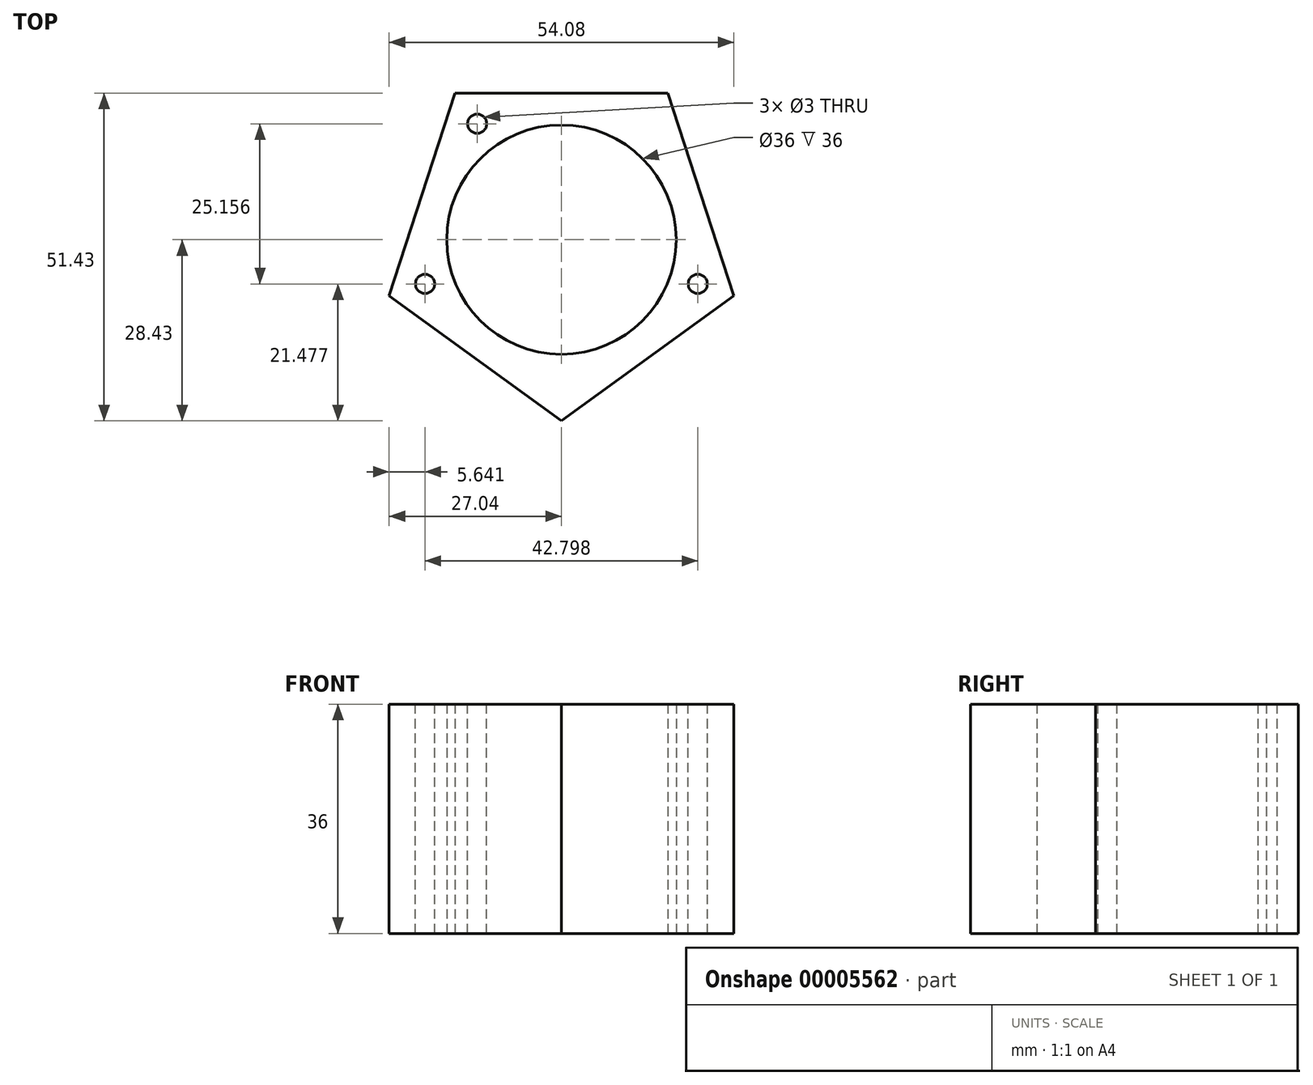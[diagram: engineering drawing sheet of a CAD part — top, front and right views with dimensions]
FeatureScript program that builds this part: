
annotation { "Feature Type Name" : "Feature", "Feature Type Description" : "" }
export const myFeature = defineFeature(function(context is Context, id is Id, definition is map)
    precondition{}
    {
        {
            var Q0;
            Q0=qCreatedBy(makeId("Top.planeOp"),FACE);
            var sketch = newSketch(context, id + "F0", { "sketchPlane" : qUnion([Q0])});
            skCircle(sketch, "E0", {"center": v(0, 0) * mm, "radius": 18 * mm});
            skCircle(sketch, "E1.cCircle", {"center": v(0, 0) * mm, "radius": 23 * mm, "construction": true});
            skLineSegment(sketch, "E1.0", {"start": v(-16.71, 23) * mm, "end": v(16.71, 23) * mm});
            skLineSegment(sketch, "E1.1", {"start": v(16.71, 23) * mm, "end": v(27.04, -8.79) * mm});
            skLineSegment(sketch, "E1.2", {"start": v(27.04, -8.79) * mm, "end": v(0, -28.43) * mm});
            skLineSegment(sketch, "E1.3", {"start": v(0, -28.43) * mm, "end": v(-27.04, -8.79) * mm});
            skLineSegment(sketch, "E1.4", {"start": v(-27.04, -8.79) * mm, "end": v(-16.71, 23) * mm});
            skPoint(sketch, "E1.0.midPoint", {"position": v(0, 23) * mm});
            skSolve(sketch);
        }
        {
            var Q0;
            Q0=qSketchRegion(id+"F0",true);
            extrude(context, id + "F1", {"entities" : qUnion([Q0]), "depth" : 36 * mm});
        }
        {
            var Q0;
            Q0=makeQuery(id+"F1.opExtrude","CAP_FACE",FACE,{"disambiguationData":[OSD([sQuery(id+"F0.wireOp",EDGE,"E0"),sQuery(id+"F0.wireOp",EDGE,"E1.0"),sQuery(id+"F0.wireOp",EDGE,"E1.1"),sQuery(id+"F0.wireOp",EDGE,"E1.2"),sQuery(id+"F0.wireOp",EDGE,"E1.3"),sQuery(id+"F0.wireOp",EDGE,"E1.4")])],"isStart":false});
            var sketch = newSketch(context, id + "F2", { "sketchPlane" : qUnion([Q0])});
            skCircle(sketch, "E2", {"center": v(0, -22.5) * mm, "radius": 1.5 * mm});
            skCircle(sketch, "E3.1.0", {"center": v(-21.4, -6.95) * mm, "radius": 1.5 * mm});
            skCircle(sketch, "E3.2.0", {"center": v(-13.23, 18.2) * mm, "radius": 1.5 * mm});
            skCircle(sketch, "E3.3.0", {"center": v(13.23, 18.2) * mm, "radius": 1.5 * mm});
            skCircle(sketch, "E3.4.0", {"center": v(21.4, -6.95) * mm, "radius": 1.5 * mm});
            skPoint(sketch, "E3.center", {"position": v(0, 0) * mm});
            skLineSegment(sketch, "E3.anchor1", {"start": v(0, 0) * mm, "end": v(0, -22.5) * mm, "construction": true});
            skLineSegment(sketch, "E3.anchor2", {"start": v(0, 0) * mm, "end": v(21.4, -6.95) * mm, "construction": true});
            skSolve(sketch);
        }
        {
            var Q0;
            Q0=makeQuery(id+"F2.imprint","IMPRINT",FACE,{"disambiguationData":[TD([[makeQuery(id+"F2.imprint","IMPRINT",EDGE,{"derivedFrom":sQuery(id+"F2.wireOp",EDGE,"E3.2.0")}),1.0]])]});
            var Q1;
            Q1=makeQuery(id+"F2.imprint","IMPRINT",FACE,{"disambiguationData":[TD([[makeQuery(id+"F2.imprint","IMPRINT",EDGE,{"derivedFrom":sQuery(id+"F2.wireOp",EDGE,"E3.4.0")}),1.0]])]});
            var Q2;
            Q2=makeQuery(id+"F2.imprint","IMPRINT",FACE,{"disambiguationData":[TD([[makeQuery(id+"F2.imprint","IMPRINT",EDGE,{"derivedFrom":sQuery(id+"F2.wireOp",EDGE,"E3.1.0")}),1.0]])]});
            extrude(context, id + "F3", {"entities" : qUnion([Q0, Q1, Q2]), "operationType" : NewBodyOperationType.REMOVE, "endBound" : BoundingType.THROUGH_ALL, "oppositeDirection" : true, "depth" : 8 * mm});
        }
    });
